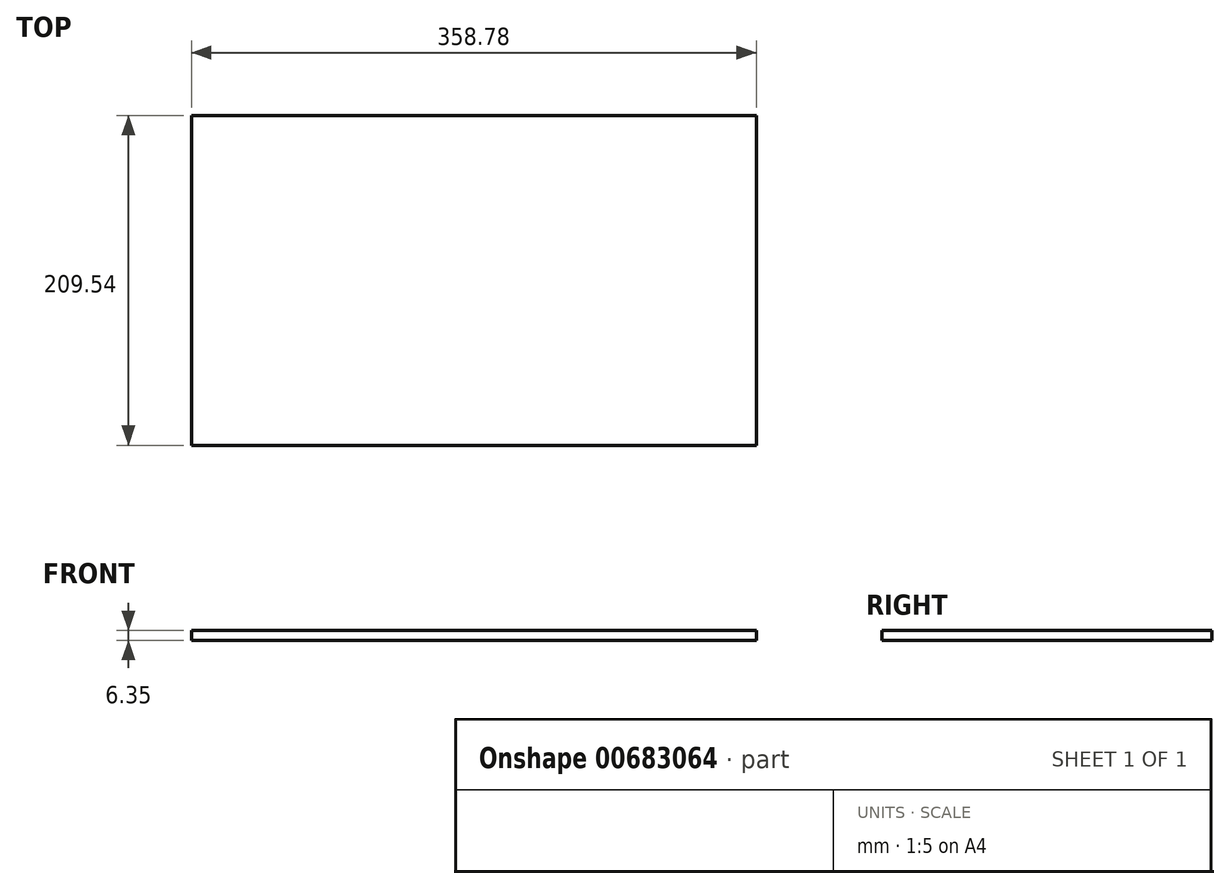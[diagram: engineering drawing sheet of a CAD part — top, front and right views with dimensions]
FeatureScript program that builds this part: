
annotation { "Feature Type Name" : "Feature", "Feature Type Description" : "" }
export const myFeature = defineFeature(function(context is Context, id is Id, definition is map)
    precondition{}
    {
        {
            var Q0;
            Q0=qCreatedBy(makeId("Top.planeOp"),FACE);
            var sketch = newSketch(context, id + "F0", { "sketchPlane" : qUnion([Q0])});
            skLineSegment(sketch, "E0.bottom", {"start": v(179.39, 104.78) * mm, "end": v(-179.39, 104.78) * mm});
            skLineSegment(sketch, "E0.top", {"start": v(179.39, -104.78) * mm, "end": v(-179.39, -104.78) * mm});
            skLineSegment(sketch, "E0.left", {"start": v(179.39, 104.78) * mm, "end": v(179.39, -104.78) * mm});
            skLineSegment(sketch, "E0.right", {"start": v(-179.39, 104.78) * mm, "end": v(-179.39, -104.78) * mm});
            skPoint(sketch, "E0.middle", {"position": v(0, 0) * mm});
            skSolve(sketch);
        }
        {
            var Q0;
            Q0 = qSketchRegion(id + "F0", true);
            extrude(context, id + "F1", {"entities" : qUnion([Q0]), "depth" : 6.35 * mm, "offsetDistance" : 25.4 * mm});
        }
    });
